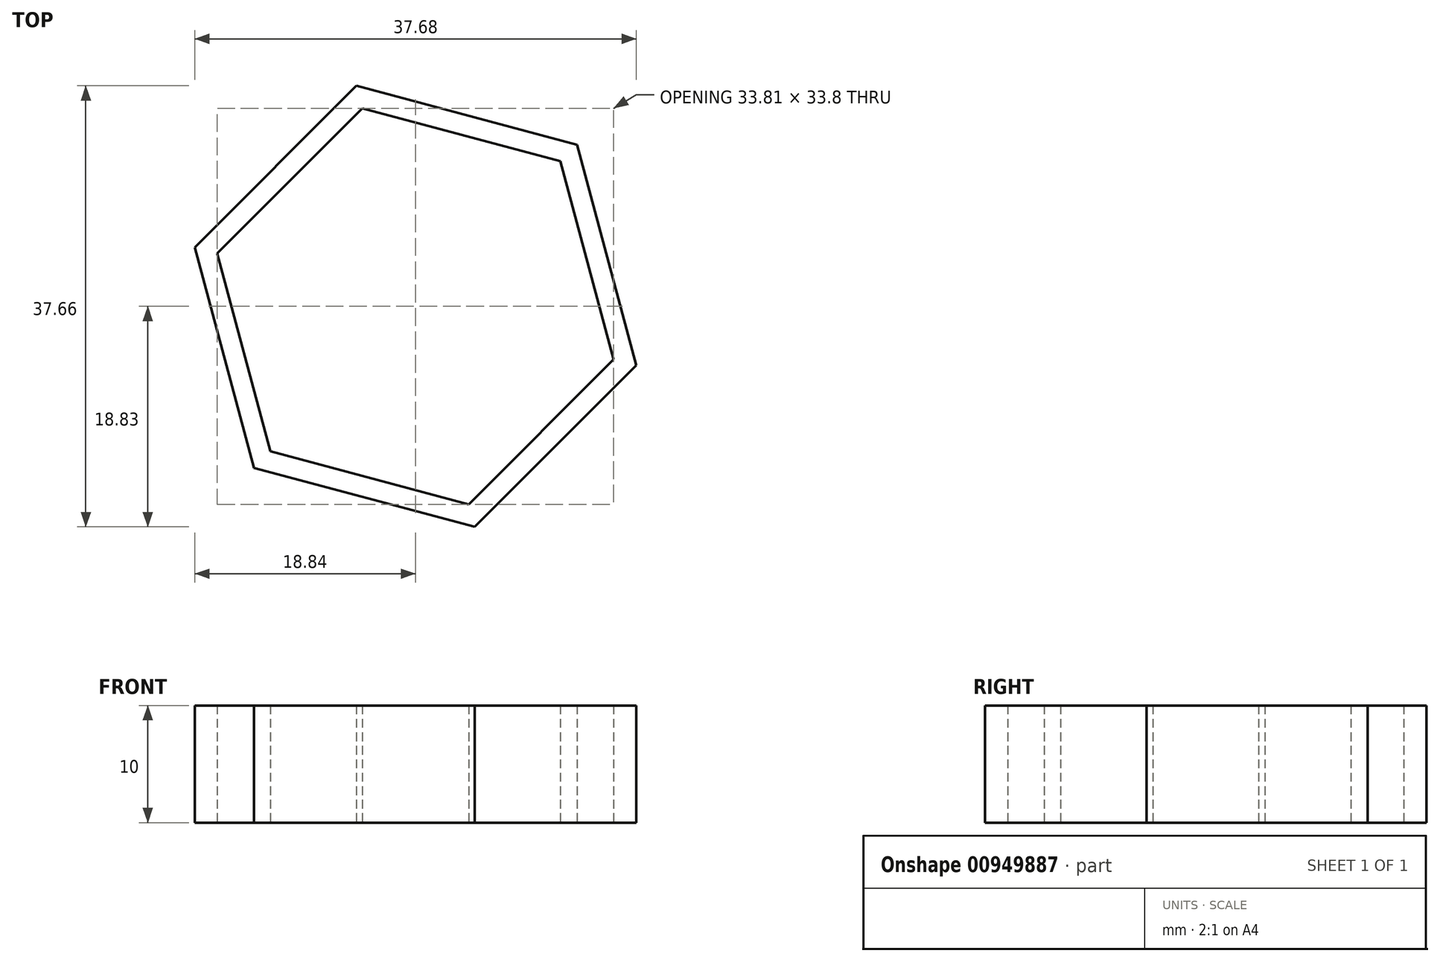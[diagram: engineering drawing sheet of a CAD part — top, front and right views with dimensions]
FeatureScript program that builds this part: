
annotation { "Feature Type Name" : "Feature", "Feature Type Description" : "" }
export const myFeature = defineFeature(function(context is Context, id is Id, definition is map)
    precondition{}
    {
        {
            var Q0;
            Q0=qCreatedBy(makeId("Top.planeOp"),FACE);
            var sketch = newSketch(context, id + "F0", { "sketchPlane" : qUnion([Q0])});
            skCircle(sketch, "E0.cCircle", {"center": v(0, 0) * mm, "radius": 15.16 * mm, "construction": true});
            skLineSegment(sketch, "E0.0", {"start": v(16.9, -4.52) * mm, "end": v(4.54, -16.9) * mm});
            skLineSegment(sketch, "E0.1", {"start": v(4.54, -16.9) * mm, "end": v(-12.37, -12.38) * mm});
            skLineSegment(sketch, "E0.2", {"start": v(-12.37, -12.38) * mm, "end": v(-16.9, 4.52) * mm});
            skLineSegment(sketch, "E0.3", {"start": v(-16.9, 4.52) * mm, "end": v(-4.54, 16.9) * mm});
            skLineSegment(sketch, "E0.4", {"start": v(-4.54, 16.9) * mm, "end": v(12.37, 12.38) * mm});
            skLineSegment(sketch, "E0.5", {"start": v(12.37, 12.38) * mm, "end": v(16.9, -4.52) * mm});
            skPoint(sketch, "E0.0.midPoint", {"position": v(10.72, -10.71) * mm});
            skCircle(sketch, "E1.cCircle", {"center": v(0, 0) * mm, "radius": 16.89 * mm, "construction": true});
            skLineSegment(sketch, "E1.0", {"start": v(18.84, -5.04) * mm, "end": v(5.06, -18.83) * mm});
            skLineSegment(sketch, "E1.1", {"start": v(5.06, -18.83) * mm, "end": v(-13.78, -13.8) * mm});
            skLineSegment(sketch, "E1.2", {"start": v(-13.78, -13.8) * mm, "end": v(-18.84, 5.04) * mm});
            skLineSegment(sketch, "E1.3", {"start": v(-18.84, 5.04) * mm, "end": v(-5.06, 18.83) * mm});
            skLineSegment(sketch, "E1.4", {"start": v(-5.06, 18.83) * mm, "end": v(13.78, 13.8) * mm});
            skLineSegment(sketch, "E1.5", {"start": v(13.78, 13.8) * mm, "end": v(18.84, -5.04) * mm});
            skPoint(sketch, "E1.0.midPoint", {"position": v(11.95, -11.93) * mm});
            skSolve(sketch);
        }
        {
            var Q0;
            Q0 = qSketchRegion(id + "F0", true);
            extrude(context, id + "F1", {"entities" : qUnion([Q0]), "depth" : 10 * mm, "offsetDistance" : 25 * mm});
        }
    });
